# Revit family: S-3200 (FlexFrame)
name_source: partatom
category: Generic Models
revit_build: Autodesk Revit Architecture 2015 (Build: 20141119_1515(x64)
units: mm (PartAtom-declared; Revit-internal decimal feet)

## types (8) — shared parameters
Description = Flexible Dock Shelter
DropCurtain = 3' - 0"
Manufacturer = Entrematic
Model = S-3200 Snapback (Flexframe)
Opening = 7' - 0"
URL = https://www.entrematic.us

## per-type parameters (varying)
| type | CurtainW | Height | HiddenHood | HoodW | Projection | Width |
| 11'-6" x 11', Standard Projection | 11' - 0" | 11' - 0" | 6' - 9" | 1' - 0" | 2' - 0" | 11' - 6" |
| 11'-6" x 11', Swing-In Projection | 11' - 0" | 11' - 0" | 6' - 9" | 1' - 0" | 2' - 4" | 11' - 6" |
| 11'-6" x 11', Standard Projection, 45 Deg Hood | 11' - 0" | 11' - 0" | 6' - 9" | 12' - 6" | 2' - 0" | 11' - 6" |
| 11'-6" x 11', Swing-In Projection, 45 Deg Hood | 11' - 0" | 11' - 0" | 6' - 9" | 12' - 6" | 2' - 4" | 11' - 6" |
| 12' x 12'-6, Standard Projection | 11' - 6" | 12' - 6" | 7' - 0" | 1' - 0" | 2' - 0" | 12' - 0" |
| 12' x 12'-6, Standard Projection, 45 Deg Hood | 11' - 6" | 12' - 6" | 7' - 0" | 13' - 0" | 2' - 0" | 12' - 0" |
| 12' x 12'-6, Swing-In Projection | 11' - 6" | 12' - 6" | 7' - 0" | 1' - 0" | 2' - 4" | 12' - 0" |
| 12' x 12'-6, Swing-In Projection, 45 Deg Hood | 11' - 6" | 12' - 6" | 7' - 0" | 13' - 0" | 2' - 4" | 12' - 0" |

## geometry (parser evidence)
native form markers: Sweep x2
no freeform markers — native parametric forms only
